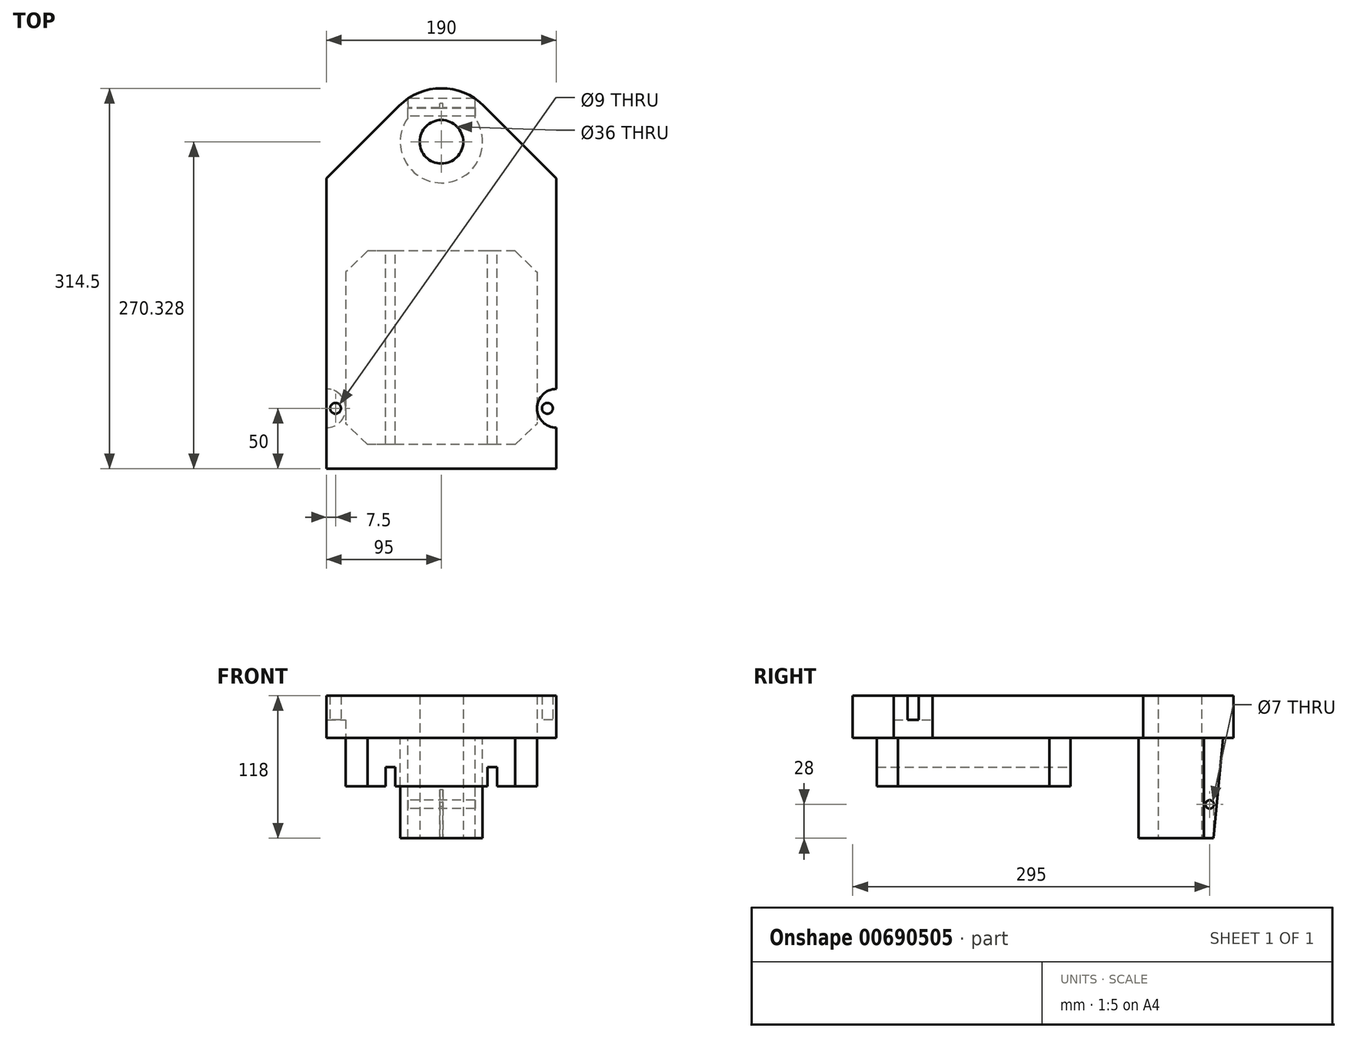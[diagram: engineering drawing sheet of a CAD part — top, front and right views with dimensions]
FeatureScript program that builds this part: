
annotation { "Feature Type Name" : "Feature", "Feature Type Description" : "" }
export const myFeature = defineFeature(function(context is Context, id is Id, definition is map)
    precondition{}
    {
        {
            var Q0;
            Q0=qCreatedBy(makeId("Top.planeOp"),FACE);
            var sketch = newSketch(context, id + "F0", { "sketchPlane" : qUnion([Q0])});
            skLineSegment(sketch, "E0", {"start": v(35, 160) * mm, "end": v(95, 100) * mm});
            skLineSegment(sketch, "E1", {"start": v(95, 100) * mm, "end": v(95, -140) * mm});
            skLineSegment(sketch, "E2", {"start": v(95, -140) * mm, "end": v(-95, -140) * mm});
            skLineSegment(sketch, "E3", {"start": v(-95, -140) * mm, "end": v(-95, 100) * mm});
            skLineSegment(sketch, "E4", {"start": v(-95, 100) * mm, "end": v(-35, 160) * mm});
            skLineSegment(sketch, "E5.bottom", {"start": v(79, 40) * mm, "end": v(-79, 40) * mm});
            skLineSegment(sketch, "E5.top", {"start": v(79, -120) * mm, "end": v(-79, -120) * mm});
            skLineSegment(sketch, "E5.left", {"start": v(79, 40) * mm, "end": v(79, -120) * mm});
            skLineSegment(sketch, "E5.right", {"start": v(-79, 40) * mm, "end": v(-79, -120) * mm});
            skPoint(sketch, "E5.middle", {"position": v(0, -40) * mm});
            skLineSegment(sketch, "E6", {"start": v(-35, 160) * mm, "end": v(35, 160) * mm});
            skArc(sketch, "E7", {"start": v(-95, -106) * mm, "mid": v(-79, -90) * mm, "end": v(-95, -74) * mm});
            skLineSegment(sketch, "E8", {"start": v(0, 211.59) * mm, "end": v(0, -212) * mm, "construction": true});
            skArc(sketch, "E9.MirrorC", {"start": v(95, -106) * mm, "mid": v(79, -90) * mm, "end": v(95, -74) * mm});
            skCircle(sketch, "E10", {"center": v(-87.5, -90) * mm, "radius": 4.5 * mm});
            skCircle(sketch, "E11.MirrorC", {"center": v(87.5, -90) * mm, "radius": 4.5 * mm});
            skSolve(sketch);
        }
        {
            var Q0;
            {var subQ9=sQuery(id+"F0.wireOp",EDGE,"E0");Q0=makeQuery(id+"F0.imprint","IMPRINT",FACE,{"disambiguationData":[TD([[makeQuery(id+"F0.imprint","IMPRINT",EDGE,{"derivedFrom":subQ9}),-1.0]])]});}
            var Q1;
            {var subQ2=sQuery(id+"F0.wireOp",EDGE,"E2");Q1=makeQuery(id+"F0.imprint","IMPRINT",FACE,{"disambiguationData":[TD([[makeQuery(id+"F0.imprint","IMPRINT",EDGE,{"derivedFrom":subQ2}),-1.0]])]});}
            var Q2;
            Q2=makeQuery(id+"F0.imprint","IMPRINT",FACE,{"disambiguationData":[TD([[makeQuery(id+"F0.imprint","IMPRINT",EDGE,{"derivedFrom":sQuery(id+"F0.wireOp",EDGE,"E10")}),-1.0]])]});
            var Q3;
            Q3=makeQuery(id+"F0.imprint","IMPRINT",FACE,{"disambiguationData":[TD([[makeQuery(id+"F0.imprint","IMPRINT",EDGE,{"derivedFrom":sQuery(id+"F0.wireOp",EDGE,"E11.MirrorC")}),1.0]])]});
            var Q4;
            {var subQ3=sQuery(id+"F0.wireOp",EDGE,"E5.bottom");Q4=makeQuery(id+"F0.imprint","IMPRINT",FACE,{"disambiguationData":[TD([[makeQuery(id+"F0.imprint","IMPRINT",EDGE,{"derivedFrom":subQ3}),1.0]])]});}
            var Q5;
            {var subQ6=sQuery(id+"F0.wireOp",EDGE,"hIP6tWcA-t8S8-ILGi-T3X6-jvU0daPei1ox");Q5=makeQuery(id+"F0.imprint","IMPRINT",FACE,{"disambiguationData":[TD([[makeQuery(id+"F0.imprint","IMPRINT",EDGE,{"derivedFrom":subQ6}),1.0]])]});}
            var Q6;
            {var subQ6=sQuery(id+"F0.wireOp",EDGE,"qTvke3HY-Selk-kILV-j3jD-UZwtlApey77z");Q6=makeQuery(id+"F0.imprint","IMPRINT",FACE,{"disambiguationData":[TD([[makeQuery(id+"F0.imprint","IMPRINT",EDGE,{"derivedFrom":subQ6}),-1.0]])]});}
            extrude(context, id + "F1", {"entities" : qUnion([Q0, Q1, Q2, Q3, Q4, Q5, Q6]), "depth" : 35 * mm, "offsetDistance" : 25 * mm});
        }
        {
            var Q0;
            {var subQ3=sQuery(id+"F0.wireOp",EDGE,"E5.bottom");Q0=makeQuery(id+"F0.imprint","IMPRINT",FACE,{"disambiguationData":[TD([[makeQuery(id+"F0.imprint","IMPRINT",EDGE,{"derivedFrom":subQ3}),1.0]])]});}
            var Q1;
            {var subQ6=sQuery(id+"F0.wireOp",EDGE,"hIP6tWcA-t8S8-ILGi-T3X6-jvU0daPei1ox");Q1=makeQuery(id+"F0.imprint","IMPRINT",FACE,{"disambiguationData":[TD([[makeQuery(id+"F0.imprint","IMPRINT",EDGE,{"derivedFrom":subQ6}),1.0]])]});}
            var Q2;
            {var subQ6=sQuery(id+"F0.wireOp",EDGE,"qTvke3HY-Selk-kILV-j3jD-UZwtlApey77z");Q2=makeQuery(id+"F0.imprint","IMPRINT",FACE,{"disambiguationData":[TD([[makeQuery(id+"F0.imprint","IMPRINT",EDGE,{"derivedFrom":subQ6}),-1.0]])]});}
            extrude(context, id + "F2", {"entities" : qUnion([Q0, Q1, Q2]), "operationType" : NewBodyOperationType.ADD, "oppositeDirection" : true, "depth" : 24 * mm, "offsetDistance" : 25 * mm});
        }
        {
            var Q0;
            Q0=makeQuery(id+"F0.imprint","IMPRINT",FACE,{"disambiguationData":[TD([[makeQuery(id+"F0.imprint","IMPRINT",EDGE,{"derivedFrom":sQuery(id+"F0.wireOp",EDGE,"E10")}),-1.0]])]});
            var Q1;
            Q1=makeQuery(id+"F0.imprint","IMPRINT",FACE,{"disambiguationData":[TD([[makeQuery(id+"F0.imprint","IMPRINT",EDGE,{"derivedFrom":sQuery(id+"F0.wireOp",EDGE,"E11.MirrorC")}),1.0]])]});
            extrude(context, id + "F3", {"entities" : qUnion([Q0, Q1]), "operationType" : NewBodyOperationType.REMOVE, "depth" : 15 * mm, "offsetDistance" : 25 * mm});
        }
        {
            var Q0;
            {var subQ0=sQuery(id+"F0.wireOp",EDGE,"E6");var subQ1=sQuery(id+"F0.wireOp",EDGE,"E4");var subQ2=sQuery(id+"F0.wireOp",EDGE,"E0");var subQ3=sQuery(id+"F0.wireOp",EDGE,"E3");var subQ4=sQuery(id+"F0.wireOp",EDGE,"E1");var subQ5=makeQuery(id+"F1.opExtrude","CAP_FACE",FACE,{"disambiguationData":[OSD([subQ2,subQ4,sQuery(id+"F0.wireOp",EDGE,"E2"),subQ3,subQ1,subQ0,sQuery(id+"F0.wireOp",EDGE,"E10"),sQuery(id+"F0.wireOp",EDGE,"E11.MirrorC")])],"isStart":true});Q0=makeQuery(id+"F3.boolean.opBoolean","SPLIT",FACE,{"disambiguationData":[TD([makeQuery(id+"F1.opExtrude","SWEPT_FACE",FACE,{"disambiguationData":[OSD([subQ2])]})])],"derivedFrom":subQ5});}
            var sketch = newSketch(context, id + "F4", { "sketchPlane" : qUnion([Q0])});
            skArc(sketch, "E12", {"start": v(-35, -160) * mm, "mid": v(0, -174.5) * mm, "end": v(35, -160) * mm});
            skSolve(sketch);
        }
        {
            var Q0;
            Q0=makeQuery(id+"F4.imprint","IMPRINT",FACE,{"disambiguationData":[TD([[makeQuery(id+"F4.imprint","IMPRINT",EDGE,{"derivedFrom":sQuery(id+"F4.wireOp",EDGE,"E12")}),1.0]])]});
            extrude(context, id + "F5", {"entities" : qUnion([Q0]), "operationType" : NewBodyOperationType.ADD, "oppositeDirection" : true, "depth" : 35 * mm, "offsetDistance" : 25 * mm});
        }
        {
            var Q0;
            {var subQ0=sQuery(id+"F0.wireOp",EDGE,"E6");var subQ1=sQuery(id+"F0.wireOp",EDGE,"E4");var subQ2=sQuery(id+"F0.wireOp",EDGE,"E0");var subQ3=sQuery(id+"F0.wireOp",EDGE,"E3");var subQ4=sQuery(id+"F0.wireOp",EDGE,"E1");var subQ5=makeQuery(id+"F1.opExtrude","CAP_FACE",FACE,{"disambiguationData":[OSD([subQ2,subQ4,sQuery(id+"F0.wireOp",EDGE,"E2"),subQ3,subQ1,subQ0,sQuery(id+"F0.wireOp",EDGE,"E10"),sQuery(id+"F0.wireOp",EDGE,"E11.MirrorC")])],"isStart":true});Q0=makeQuery(id+"F5.boolean.opBoolean","MERGE",FACE,{"derivedFrom":[makeQuery(id+"F3.boolean.opBoolean","SPLIT",FACE,{"disambiguationData":[TD([makeQuery(id+"F1.opExtrude","SWEPT_FACE",FACE,{"disambiguationData":[OSD([subQ2])]})])],"derivedFrom":subQ5}),makeQuery(id+"F5.opExtrude","CAP_FACE",FACE,{"disambiguationData":[OSD([subQ0,sQuery(id+"F4.wireOp",EDGE,"E12")])],"isStart":true})]});}
            var sketch = newSketch(context, id + "F6", { "sketchPlane" : qUnion([Q0])});
            skLineSegment(sketch, "E13.top", {"start": v(27.73, -166) * mm, "end": v(-27.73, -166) * mm});
            skLineSegment(sketch, "E13.left", {"start": v(27.73, -150) * mm, "end": v(27.73, -166) * mm});
            skLineSegment(sketch, "E13.right", {"start": v(-27.73, -150) * mm, "end": v(-27.73, -166) * mm});
            skPoint(sketch, "E13.middle", {"position": v(0, -158) * mm});
            skArc(sketch, "E14", {"start": v(27.73, -150) * mm, "mid": v(0, -96.33) * mm, "end": v(-27.73, -150) * mm});
            skSolve(sketch);
        }
        {
            var Q0;
            Q0=makeQuery(id+"F6.imprint","IMPRINT",FACE,{"disambiguationData":[TD([[makeQuery(id+"F6.imprint","IMPRINT",EDGE,{"derivedFrom":sQuery(id+"F6.wireOp",EDGE,"E13.top")}),-1.0]])]});
            extrude(context, id + "F7", {"entities" : qUnion([Q0]), "operationType" : NewBodyOperationType.ADD, "depth" : 83 * mm, "offsetDistance" : 25 * mm});
        }
        {
            var Q0;
            Q0=makeQuery(id+"F7.opExtrude","SWEPT_FACE",FACE,{"disambiguationData":[OSD([sQuery(id+"F6.wireOp",EDGE,"E13.right")])]});
            var sketch = newSketch(context, id + "F8", { "sketchPlane" : qUnion([Q0])});
            skLineSegment(sketch, "E15", {"start": v(-166, 0) * mm, "end": v(-158, -83) * mm});
            skCircle(sketch, "E16", {"center": v(-155, -55) * mm, "radius": 3.5 * mm});
            skSolve(sketch);
        }
        {
            var Q0;
            {var subQ0=sQuery(id+"F8.wireOp",EDGE,"E15");Q0=makeQuery(id+"F8.imprint","IMPRINT",FACE,{"disambiguationData":[TD([[makeQuery(id+"F8.imprint","IMPRINT",EDGE,{"derivedFrom":subQ0}),-1.0]])]});}
            extrude(context, id + "F9", {"entities" : qUnion([Q0]), "operationType" : NewBodyOperationType.REMOVE, "oppositeDirection" : true, "depth" : 290 * mm, "offsetDistance" : 25 * mm});
        }
        {
            var Q0;
            Q0=makeQuery(id+"F7.opExtrude","CAP_FACE",FACE,{"disambiguationData":[OSD([sQuery(id+"F6.wireOp",EDGE,"E13.top"),sQuery(id+"F6.wireOp",EDGE,"E13.left"),sQuery(id+"F6.wireOp",EDGE,"E13.right"),sQuery(id+"F6.wireOp",EDGE,"E14")])],"isStart":false});
            var sketch = newSketch(context, id + "F10", { "sketchPlane" : qUnion([Q0])});
            skCircle(sketch, "E17", {"center": v(0, -130.33) * mm, "radius": 18 * mm});
            skSolve(sketch);
        }
        {
            var Q0;
            Q0=makeQuery(id+"F10.imprint","IMPRINT",FACE,{"disambiguationData":[TD([[makeQuery(id+"F10.imprint","IMPRINT",EDGE,{"derivedFrom":sQuery(id+"F10.wireOp",EDGE,"E17")}),1.0]])]});
            extrude(context, id + "F11", {"entities" : qUnion([Q0]), "operationType" : NewBodyOperationType.REMOVE, "oppositeDirection" : true, "depth" : 199 * mm, "offsetDistance" : 25 * mm});
        }
        {
            var Q0;
            Q0=makeQuery(id+"F7.opExtrude","CAP_FACE",FACE,{"disambiguationData":[OSD([sQuery(id+"F6.wireOp",EDGE,"E13.top"),sQuery(id+"F6.wireOp",EDGE,"E13.left"),sQuery(id+"F6.wireOp",EDGE,"E13.right"),sQuery(id+"F6.wireOp",EDGE,"E14")])],"isStart":false});
            var sketch = newSketch(context, id + "F12", { "sketchPlane" : qUnion([Q0])});
            skLineSegment(sketch, "E18.bottom", {"start": v(-1.25, -140) * mm, "end": v(1.25, -140) * mm});
            skLineSegment(sketch, "E18.top", {"start": v(-1.25, -190) * mm, "end": v(1.25, -190) * mm});
            skLineSegment(sketch, "E18.left", {"start": v(-1.25, -140) * mm, "end": v(-1.25, -190) * mm});
            skLineSegment(sketch, "E18.right", {"start": v(1.25, -140) * mm, "end": v(1.25, -190) * mm});
            skPoint(sketch, "E18.middle", {"position": v(0, -165) * mm});
            skSolve(sketch);
        }
        {
            var Q0;
            {var subQ0=sQuery(id+"F12.wireOp",EDGE,"E18.top");Q0=makeQuery(id+"F12.imprint","IMPRINT",FACE,{"disambiguationData":[TD([[makeQuery(id+"F12.imprint","IMPRINT",EDGE,{"derivedFrom":subQ0}),1.0]])]});}
            var Q1;
            {var subQ0=sQuery(id+"F12.wireOp",EDGE,"E18.left");var subQ3=makeQuery(id+"F11.boolean.opBoolean","COPY",EDGE,{"derivedFrom":makeQuery(id+"F11.opExtrude","CAP_EDGE",EDGE,{"disambiguationData":[OSD([sQuery(id+"F10.wireOp",EDGE,"E17")])],"isStart":true})});var subQ4=makeQuery(id+"F12.imprint","INTERSECT",VERTEX,{"derivedFrom":[subQ3,subQ0]});Q1=makeQuery(id+"F12.imprint","IMPRINT",FACE,{"disambiguationData":[TD([[makeQuery(id+"F12.imprint","IMPRINT",EDGE,{"disambiguationData":[TD([[subQ4,-1.0]])],"derivedFrom":subQ3}),-1.0]])]});}
            extrude(context, id + "F13", {"entities" : qUnion([Q0, Q1]), "operationType" : NewBodyOperationType.REMOVE, "oppositeDirection" : true, "depth" : 40 * mm, "offsetDistance" : 25 * mm});
        }
        {
            var Q0;
            Q0=makeQuery(id+"F8.imprint","IMPRINT",FACE,{"disambiguationData":[TD([[makeQuery(id+"F8.imprint","IMPRINT",EDGE,{"derivedFrom":sQuery(id+"F8.wireOp",EDGE,"E16")}),1.0]])]});
            extrude(context, id + "F14", {"entities" : qUnion([Q0]), "operationType" : NewBodyOperationType.REMOVE, "oppositeDirection" : true, "depth" : 99.1 * mm, "offsetDistance" : 25 * mm});
        }
        {
            var Q0;
            Q0=makeQuery(id+"F2.opExtrude","CAP_FACE",FACE,{"disambiguationData":[OSD([sQuery(id+"F0.wireOp",EDGE,"E5.bottom"),sQuery(id+"F0.wireOp",EDGE,"E5.top"),sQuery(id+"F0.wireOp",EDGE,"E5.left"),sQuery(id+"F0.wireOp",EDGE,"E5.right")])],"isStart":false});
            var sketch = newSketch(context, id + "F15", { "sketchPlane" : qUnion([Q0])});
            skLineSegment(sketch, "E19", {"start": v(-46, 120) * mm, "end": v(-46, -40) * mm});
            skLineSegment(sketch, "E20", {"start": v(-38, 120) * mm, "end": v(-38, -40) * mm});
            skLineSegment(sketch, "E21.MirrorCS", {"start": v(38, 120) * mm, "end": v(38, -40) * mm});
            skLineSegment(sketch, "E22.MirrorCS", {"start": v(46, 120) * mm, "end": v(46, -40) * mm});
            skLineSegment(sketch, "E23", {"start": v(-61, 120) * mm, "end": v(-79, 102.65) * mm});
            skLineSegment(sketch, "E24", {"start": v(-61, -40) * mm, "end": v(-79, -22.65) * mm});
            skLineSegment(sketch, "E25.MirrorCS", {"start": v(61, -40) * mm, "end": v(79, -22.65) * mm});
            skLineSegment(sketch, "E26.MirrorCS", {"start": v(61, 120) * mm, "end": v(79, 102.65) * mm});
            skSolve(sketch);
        }
        {
            var Q0;
            {var subQ0=sQuery(id+"F15.wireOp",EDGE,"E19");Q0=makeQuery(id+"F15.imprint","IMPRINT",FACE,{"disambiguationData":[TD([[makeQuery(id+"F15.imprint","IMPRINT",EDGE,{"derivedFrom":subQ0}),-1.0]])]});}
            var Q1;
            {var subQ0=sQuery(id+"F15.wireOp",EDGE,"E20");Q1=makeQuery(id+"F15.imprint","IMPRINT",FACE,{"disambiguationData":[TD([[makeQuery(id+"F15.imprint","IMPRINT",EDGE,{"derivedFrom":subQ0}),1.0]])]});}
            var Q2;
            {var subQ0=sQuery(id+"F15.wireOp",EDGE,"E22.MirrorCS");Q2=makeQuery(id+"F15.imprint","IMPRINT",FACE,{"disambiguationData":[TD([[makeQuery(id+"F15.imprint","IMPRINT",EDGE,{"derivedFrom":subQ0}),1.0]])]});}
            extrude(context, id + "F16", {"entities" : qUnion([Q0, Q1, Q2]), "operationType" : NewBodyOperationType.ADD, "depth" : 16 * mm, "offsetDistance" : 25 * mm});
        }
        {
            var Q0;
            {var subQ0=sQuery(id+"F15.wireOp",EDGE,"E24");Q0=makeQuery(id+"F15.imprint","IMPRINT",FACE,{"disambiguationData":[TD([[makeQuery(id+"F15.imprint","IMPRINT",EDGE,{"derivedFrom":subQ0}),1.0]])]});}
            var Q1;
            {var subQ0=sQuery(id+"F15.wireOp",EDGE,"E23");Q1=makeQuery(id+"F15.imprint","IMPRINT",FACE,{"disambiguationData":[TD([[makeQuery(id+"F15.imprint","IMPRINT",EDGE,{"derivedFrom":subQ0}),-1.0]])]});}
            var Q2;
            {var subQ0=sQuery(id+"F15.wireOp",EDGE,"E26.MirrorCS");Q2=makeQuery(id+"F15.imprint","IMPRINT",FACE,{"disambiguationData":[TD([[makeQuery(id+"F15.imprint","IMPRINT",EDGE,{"derivedFrom":subQ0}),1.0]])]});}
            var Q3;
            {var subQ0=sQuery(id+"F15.wireOp",EDGE,"E25.MirrorCS");Q3=makeQuery(id+"F15.imprint","IMPRINT",FACE,{"disambiguationData":[TD([[makeQuery(id+"F15.imprint","IMPRINT",EDGE,{"derivedFrom":subQ0}),-1.0]])]});}
            extrude(context, id + "F17", {"entities" : qUnion([Q0, Q1, Q2, Q3]), "operationType" : NewBodyOperationType.REMOVE, "oppositeDirection" : true, "depth" : 24 * mm, "offsetDistance" : 25 * mm});
        }
    });
